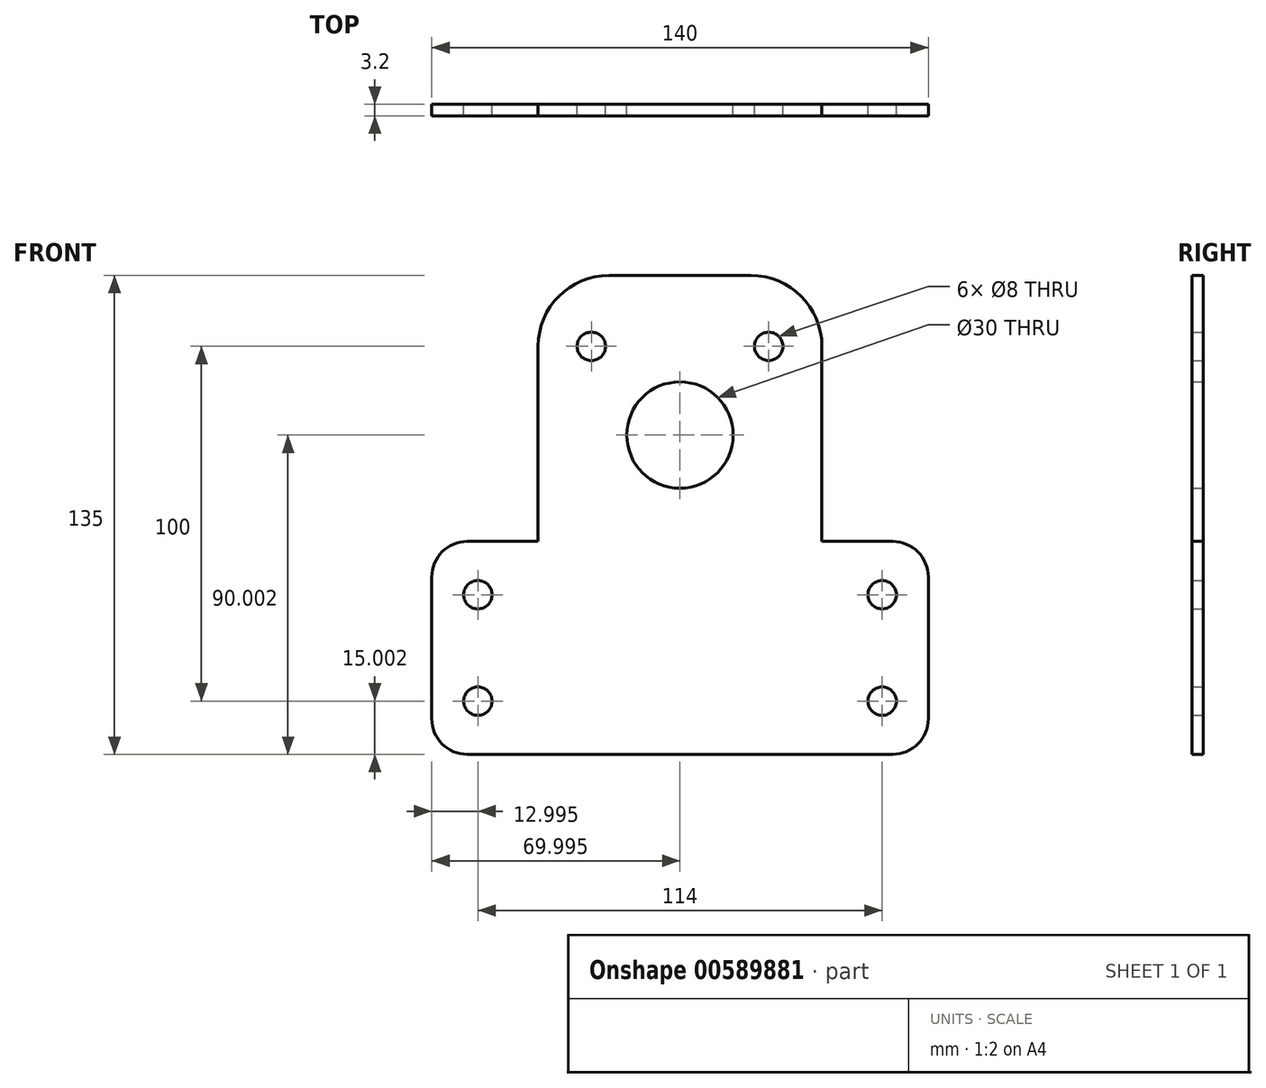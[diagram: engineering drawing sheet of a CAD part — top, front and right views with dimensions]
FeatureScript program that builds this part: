
annotation { "Feature Type Name" : "Feature", "Feature Type Description" : "" }
export const myFeature = defineFeature(function(context is Context, id is Id, definition is map)
    precondition{}
    {
        {
            var Q0;
            Q0=qCreatedBy(makeId("Top.planeOp"),FACE);
            var sketch = newSketch(context, id + "F0", { "sketchPlane" : qUnion([Q0])});
            skLineSegment(sketch, "E0", {"start": v(-60.77, -19.8) * mm, "end": v(-32.77, -19.8) * mm});
            skLineSegment(sketch, "E1", {"start": v(-30.77, -17.8) * mm, "end": v(-30.77, 18.2) * mm});
            skLineSegment(sketch, "E2", {"start": v(-28.77, 20.2) * mm, "end": v(47.23, 20.2) * mm});
            skLineSegment(sketch, "E3", {"start": v(49.23, 18.2) * mm, "end": v(49.23, -17.8) * mm});
            skLineSegment(sketch, "E4", {"start": v(51.23, -19.8) * mm, "end": v(79.23, -19.8) * mm});
            skLineSegment(sketch, "E5.0", {"start": v(54.23, -16.8) * mm, "end": v(79.23, -16.8) * mm});
            skLineSegment(sketch, "E5.1", {"start": v(-60.77, -16.8) * mm, "end": v(-35.77, -16.8) * mm});
            skLineSegment(sketch, "E5.2", {"start": v(-33.77, -14.8) * mm, "end": v(-33.77, 23.2) * mm});
            skLineSegment(sketch, "E5.3", {"start": v(-33.77, 23.2) * mm, "end": v(50.23, 23.2) * mm});
            skLineSegment(sketch, "E5.4", {"start": v(52.23, 21.2) * mm, "end": v(52.23, -14.8) * mm});
            skLineSegment(sketch, "E6", {"start": v(-60.77, -19.8) * mm, "end": v(-60.77, -16.8) * mm});
            skLineSegment(sketch, "E7", {"start": v(79.23, -19.8) * mm, "end": v(79.23, -16.8) * mm});
            skLineSegment(sketch, "E8", {"start": v(-32.58, 23.2) * mm, "end": v(-33.77, 21.59) * mm});
            skPoint(sketch, "E9.visualSharp", {"position": v(52.23, 23.2) * mm});
            skArc(sketch, "E9.filletArc", {"start": v(52.23, 21.2) * mm, "mid": v(51.64, 22.6) * mm, "end": v(50.23, 23.2) * mm});
            skPoint(sketch, "E10.visualSharp", {"position": v(49.23, 20.2) * mm});
            skArc(sketch, "E10.filletArc", {"start": v(49.23, 18.2) * mm, "mid": v(48.64, 19.6) * mm, "end": v(47.23, 20.2) * mm});
            skPoint(sketch, "E11.visualSharp", {"position": v(-30.77, 20.2) * mm});
            skArc(sketch, "E11.filletArc", {"start": v(-28.77, 20.2) * mm, "mid": v(-30.18, 19.6) * mm, "end": v(-30.77, 18.2) * mm});
            skPoint(sketch, "E12.visualSharp", {"position": v(-33.77, -16.8) * mm});
            skArc(sketch, "E12.filletArc", {"start": v(-35.77, -16.8) * mm, "mid": v(-34.36, -16.22) * mm, "end": v(-33.77, -14.8) * mm});
            skPoint(sketch, "E13.visualSharp", {"position": v(-30.77, -19.8) * mm});
            skArc(sketch, "E13.filletArc", {"start": v(-32.77, -19.8) * mm, "mid": v(-31.36, -19.22) * mm, "end": v(-30.77, -17.8) * mm});
            skPoint(sketch, "E14.visualSharp", {"position": v(49.23, -19.8) * mm});
            skArc(sketch, "E14.filletArc", {"start": v(49.23, -17.8) * mm, "mid": v(49.82, -19.22) * mm, "end": v(51.23, -19.8) * mm});
            skPoint(sketch, "E15.visualSharp", {"position": v(52.23, -16.8) * mm});
            skArc(sketch, "E15.filletArc", {"start": v(52.23, -14.8) * mm, "mid": v(52.82, -16.22) * mm, "end": v(54.23, -16.8) * mm});
            skSolve(sketch);
        }
        {
            var Q0;
            Q0=qCreatedBy(makeId("Front.planeOp"),FACE);
            cPlane(context, id + "F1", {"entities" : qUnion([Q0]), "cplaneType" : CPlaneType.OFFSET, "offset" : 21 * mm, "width" : 150 * mm, "height" : 150 * mm});
        }
        {
            var Q0;
            Q0=qCreatedBy(id+"F1.planeOp",FACE);
            var sketch = newSketch(context, id + "F2", { "sketchPlane" : qUnion([Q0])});
            skLineSegment(sketch, "E16.bottom", {"start": v(-51.8, 60.16) * mm, "end": v(-31.8, 60.16) * mm});
            skLineSegment(sketch, "E16.top", {"start": v(-51.8, 0.16) * mm, "end": v(68.2, 0.16) * mm});
            skLineSegment(sketch, "E16.left", {"start": v(-61.8, 50.16) * mm, "end": v(-61.8, 10.16) * mm});
            skLineSegment(sketch, "E16.right", {"start": v(78.2, 50.16) * mm, "end": v(78.2, 10.16) * mm});
            skPoint(sketch, "E17.visualSharp", {"position": v(-61.8, 60.16) * mm});
            skArc(sketch, "E17.filletArc", {"start": v(-51.8, 60.16) * mm, "mid": v(-58.87, 57.23) * mm, "end": v(-61.8, 50.16) * mm});
            skPoint(sketch, "E18.visualSharp", {"position": v(-61.8, 0.16) * mm});
            skArc(sketch, "E18.filletArc", {"start": v(-61.8, 10.16) * mm, "mid": v(-58.87, 3.1) * mm, "end": v(-51.8, 0.16) * mm});
            skPoint(sketch, "E19.visualSharp", {"position": v(78.2, 0.16) * mm});
            skArc(sketch, "E19.filletArc", {"start": v(68.2, 0.16) * mm, "mid": v(75.28, 3.1) * mm, "end": v(78.2, 10.16) * mm});
            skPoint(sketch, "E20.visualSharp", {"position": v(78.2, 60.16) * mm});
            skArc(sketch, "E20.filletArc", {"start": v(78.2, 50.16) * mm, "mid": v(75.28, 57.23) * mm, "end": v(68.2, 60.16) * mm});
            skCircle(sketch, "E21", {"center": v(-48.8, 45.16) * mm, "radius": 4 * mm});
            skCircle(sketch, "E22", {"center": v(-48.8, 15.16) * mm, "radius": 4 * mm});
            skCircle(sketch, "E23", {"center": v(65.2, 15.16) * mm, "radius": 4 * mm});
            skCircle(sketch, "E24", {"center": v(65.2, 45.16) * mm, "radius": 4 * mm});
            skLineSegment(sketch, "E25.top", {"start": v(-11.8, 135.16) * mm, "end": v(28.2, 135.16) * mm});
            skLineSegment(sketch, "E25.left", {"start": v(-31.8, 60.16) * mm, "end": v(-31.8, 115.16) * mm});
            skLineSegment(sketch, "E25.right", {"start": v(48.2, 60.16) * mm, "end": v(48.2, 115.16) * mm});
            skPoint(sketch, "E26.visualSharp", {"position": v(-31.8, 135.16) * mm});
            skArc(sketch, "E26.filletArc", {"start": v(-11.8, 135.16) * mm, "mid": v(-25.94, 129.3) * mm, "end": v(-31.8, 115.16) * mm});
            skPoint(sketch, "E27.visualSharp", {"position": v(48.2, 135.16) * mm});
            skArc(sketch, "E27.filletArc", {"start": v(48.2, 115.16) * mm, "mid": v(42.35, 129.3) * mm, "end": v(28.2, 135.16) * mm});
            skCircle(sketch, "E28", {"center": v(-16.8, 115.16) * mm, "radius": 4 * mm});
            skCircle(sketch, "E29", {"center": v(33.2, 115.16) * mm, "radius": 4 * mm});
            skCircle(sketch, "E30", {"center": v(8.2, 90.16) * mm, "radius": 15 * mm});
            skLineSegment(sketch, "E31.trimOffspring", {"start": v(48.2, 60.16) * mm, "end": v(68.2, 60.16) * mm});
            skSolve(sketch);
        }
        {
            var Q0;
            Q0=qSketchRegion(id+"F2",true);
            extrude(context, id + "F3", {"entities" : qUnion([Q0]), "depth" : 3.2 * mm, "offsetDistance" : 25 * mm});
        }
    });
